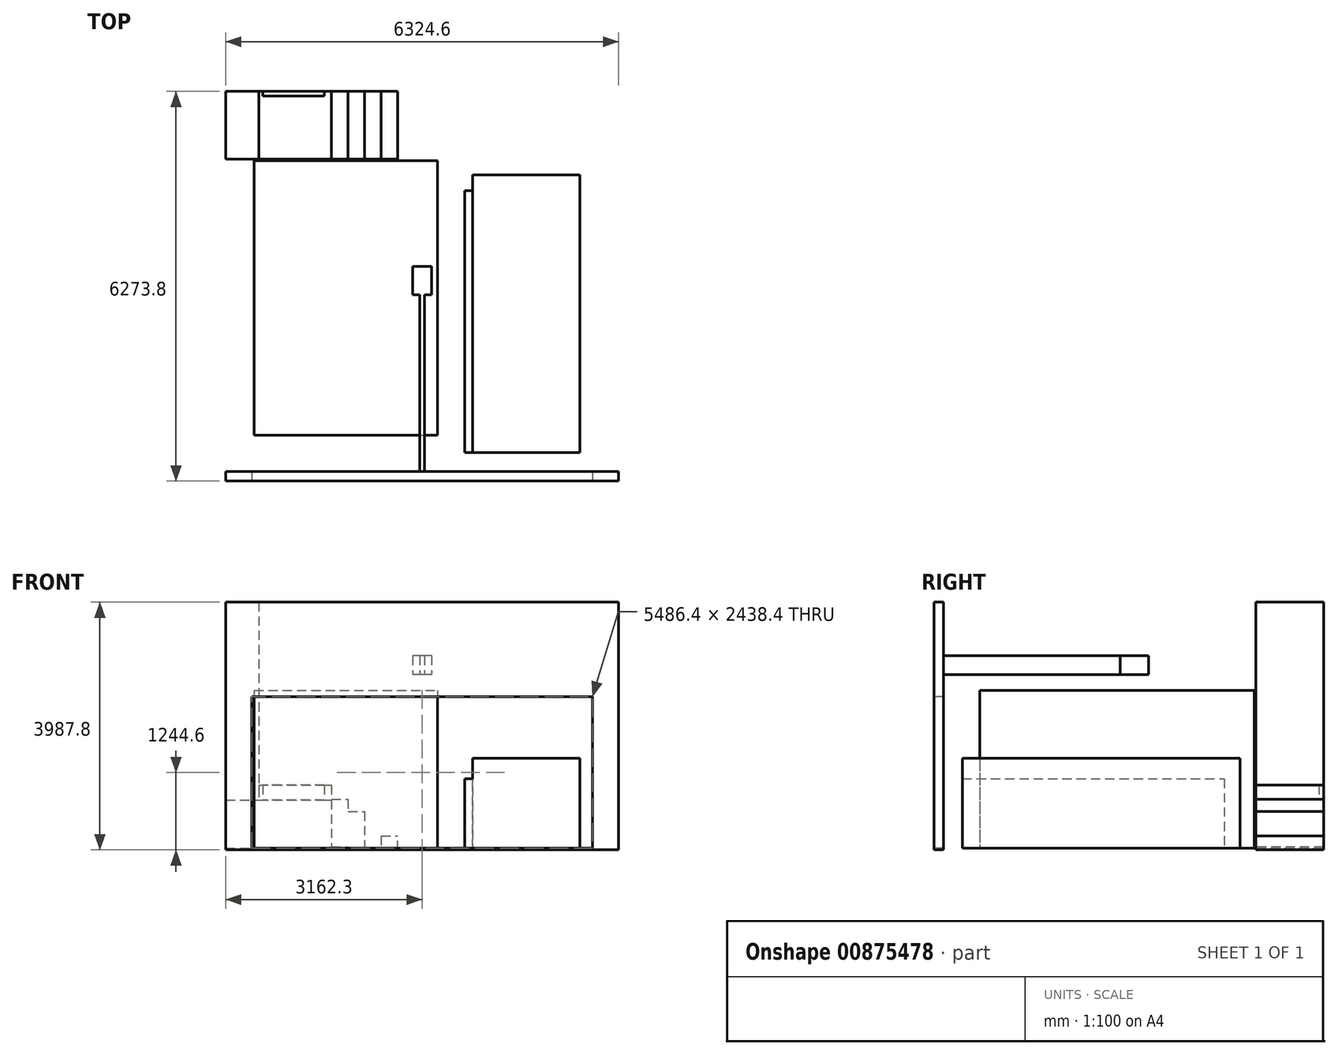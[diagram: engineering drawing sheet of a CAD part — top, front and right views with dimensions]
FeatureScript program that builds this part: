
annotation { "Feature Type Name" : "Feature", "Feature Type Description" : "" }
export const myFeature = defineFeature(function(context is Context, id is Id, definition is map)
    precondition{}
    {
        {
            var Q0;
            Q0=qCreatedBy(makeId("Top.planeOp"),FACE);
            var sketch = newSketch(context, id + "F0", { "sketchPlane" : qUnion([Q0])});
            skLineSegment(sketch, "E0.bottom", {"start": v(-3162.3, 3098.8) * mm, "end": v(3162.3, 3098.8) * mm});
            skLineSegment(sketch, "E0.top", {"start": v(-3162.3, -3098.8) * mm, "end": v(3162.3, -3098.8) * mm});
            skLineSegment(sketch, "E0.left", {"start": v(-3162.3, 3098.8) * mm, "end": v(-3162.3, -3098.8) * mm});
            skLineSegment(sketch, "E0.right", {"start": v(3162.3, 3098.8) * mm, "end": v(3162.3, -3098.8) * mm});
            skLineSegment(sketch, "E1.bottom", {"start": v(-3162.3, 3098.8) * mm, "end": v(-2628.9, 3098.8) * mm});
            skLineSegment(sketch, "E1.top", {"start": v(-3162.3, 2006.6) * mm, "end": v(-2628.9, 2006.6) * mm});
            skLineSegment(sketch, "E1.left", {"start": v(-3162.3, 3098.8) * mm, "end": v(-3162.3, 2006.6) * mm});
            skLineSegment(sketch, "E1.right", {"start": v(-2628.9, 3098.8) * mm, "end": v(-2628.9, 2006.6) * mm});
            skLineSegment(sketch, "E2.bottom", {"start": v(-2628.9, 2006.6) * mm, "end": v(-393.7, 2006.6) * mm});
            skLineSegment(sketch, "E2.top", {"start": v(-2628.9, 3098.8) * mm, "end": v(-393.7, 3098.8) * mm});
            skLineSegment(sketch, "E2.left", {"start": v(-2628.9, 2006.6) * mm, "end": v(-2628.9, 3098.8) * mm});
            skLineSegment(sketch, "E2.right", {"start": v(-393.7, 2006.6) * mm, "end": v(-393.7, 3098.8) * mm});
            skLineSegment(sketch, "E3.bottom", {"start": v(-1460.5, 3098.8) * mm, "end": v(-393.7, 3098.8) * mm});
            skLineSegment(sketch, "E3.top", {"start": v(-1460.5, 2006.6) * mm, "end": v(-393.7, 2006.6) * mm});
            skLineSegment(sketch, "E3.left", {"start": v(-1460.5, 3098.8) * mm, "end": v(-1460.5, 2006.6) * mm});
            skLineSegment(sketch, "E3.right", {"start": v(-393.7, 3098.8) * mm, "end": v(-393.7, 2006.6) * mm});
            skLineSegment(sketch, "E4.bottom", {"start": v(2743.2, -3022.6) * mm, "end": v(-2743.2, -3022.6) * mm});
            skLineSegment(sketch, "E4.top", {"start": v(2743.2, -3175) * mm, "end": v(-2743.2, -3175) * mm});
            skLineSegment(sketch, "E4.left", {"start": v(2743.2, -3022.6) * mm, "end": v(2743.2, -3175) * mm});
            skLineSegment(sketch, "E4.right", {"start": v(-2743.2, -3022.6) * mm, "end": v(-2743.2, -3175) * mm});
            skPoint(sketch, "E4.middle", {"position": v(0, -3098.8) * mm});
            skLineSegment(sketch, "E5.bottom", {"start": v(3238.5, -2006.6) * mm, "end": v(3086.1, -2006.6) * mm});
            skLineSegment(sketch, "E5.top", {"start": v(3238.5, -2921) * mm, "end": v(3086.1, -2921) * mm});
            skLineSegment(sketch, "E5.left", {"start": v(3238.5, -2006.6) * mm, "end": v(3238.5, -2921) * mm});
            skLineSegment(sketch, "E5.right", {"start": v(3086.1, -2006.6) * mm, "end": v(3086.1, -2921) * mm});
            skPoint(sketch, "E5.middle", {"position": v(3162.3, -2463.8) * mm});
            skLineSegment(sketch, "E6.bottom", {"start": v(-1576.66, 3175) * mm, "end": v(-2567.26, 3175) * mm});
            skLineSegment(sketch, "E6.top", {"start": v(-1576.66, 3022.6) * mm, "end": v(-2567.26, 3022.6) * mm});
            skLineSegment(sketch, "E6.left", {"start": v(-1576.66, 3175) * mm, "end": v(-1576.66, 3022.6) * mm});
            skLineSegment(sketch, "E6.right", {"start": v(-2567.26, 3175) * mm, "end": v(-2567.26, 3022.6) * mm});
            skPoint(sketch, "E6.middle", {"position": v(-2071.96, 3098.8) * mm});
            skLineSegment(sketch, "E7", {"start": v(-1193.8, 3098.8) * mm, "end": v(-1193.8, 2006.6) * mm});
            skLineSegment(sketch, "E8", {"start": v(-927.1, 3098.8) * mm, "end": v(-927.1, 2006.6) * mm});
            skLineSegment(sketch, "E9", {"start": v(-660.4, 2006.6) * mm, "end": v(-660.4, 3098.8) * mm});
            skSolve(sketch);
        }
        {
            var Q0;
            {var subQ3=sQuery(id+"F0.wireOp",EDGE,"E1.top");Q0=makeQuery(id+"F0.imprint","IMPRINT",FACE,{"disambiguationData":[TD([[makeQuery(id+"F0.imprint","IMPRINT",EDGE,{"derivedFrom":subQ3}),-1.0]])]});}
            var Q1;
            {var subQ4=sQuery(id+"F0.wireOp",EDGE,"E1.top");Q1=makeQuery(id+"F0.imprint","IMPRINT",FACE,{"disambiguationData":[TD([[makeQuery(id+"F0.imprint","IMPRINT",EDGE,{"derivedFrom":subQ4}),1.0]])]});}
            var Q2;
            {var subQ1=sQuery(id+"F0.wireOp",EDGE,"E1.right");Q2=makeQuery(id+"F0.imprint","IMPRINT",FACE,{"disambiguationData":[TD([[makeQuery(id+"F0.imprint","IMPRINT",EDGE,{"derivedFrom":subQ1}),1.0]])]});}
            var Q3;
            {var subQ0=sQuery(id+"F0.wireOp",EDGE,"E3.left");Q3=makeQuery(id+"F0.imprint","IMPRINT",FACE,{"disambiguationData":[TD([[makeQuery(id+"F0.imprint","IMPRINT",EDGE,{"derivedFrom":subQ0}),1.0]])]});}
            var Q4;
            {var subQ0=sQuery(id+"F0.wireOp",EDGE,"E7");Q4=makeQuery(id+"F0.imprint","IMPRINT",FACE,{"disambiguationData":[TD([[makeQuery(id+"F0.imprint","IMPRINT",EDGE,{"derivedFrom":subQ0}),1.0]])]});}
            var Q5;
            {var subQ0=sQuery(id+"F0.wireOp",EDGE,"E8");Q5=makeQuery(id+"F0.imprint","IMPRINT",FACE,{"disambiguationData":[TD([[makeQuery(id+"F0.imprint","IMPRINT",EDGE,{"derivedFrom":subQ0}),1.0]])]});}
            var Q6;
            {var subQ0=sQuery(id+"F0.wireOp",EDGE,"E2.right");Q6=makeQuery(id+"F0.imprint","IMPRINT",FACE,{"disambiguationData":[TD([[makeQuery(id+"F0.imprint","IMPRINT",EDGE,{"derivedFrom":subQ0}),1.0]])]});}
            var Q7;
            {var subQ5=sQuery(id+"F0.wireOp",EDGE,"E6.top");Q7=makeQuery(id+"F0.imprint","IMPRINT",FACE,{"disambiguationData":[TD([[makeQuery(id+"F0.imprint","IMPRINT",EDGE,{"derivedFrom":subQ5}),-1.0]])]});}
            extrude(context, id + "F1", {"entities" : qUnion([Q0, Q1, Q2, Q3, Q4, Q5, Q6, Q7]), "oppositeDirection" : true, "depth" : 25.4 * mm, "offsetDistance" : 25.4 * mm});
        }
        {
            var Q0;
            {var subQ4=sQuery(id+"F0.wireOp",EDGE,"E1.top");Q0=makeQuery(id+"F0.imprint","IMPRINT",FACE,{"disambiguationData":[TD([[makeQuery(id+"F0.imprint","IMPRINT",EDGE,{"derivedFrom":subQ4}),1.0]])]});}
            extrude(context, id + "F2", {"entities" : qUnion([Q0]), "depth" : 3962.4 * mm, "offsetDistance" : 25.4 * mm, "hasSecondDirection" : true, "secondDirectionOppositeDirection" : false, "secondDirectionDepth" : 774.7 * mm});
        }
        {
            var Q0;
            {var subQ1=sQuery(id+"F0.wireOp",EDGE,"E1.right");Q0=makeQuery(id+"F0.imprint","IMPRINT",FACE,{"disambiguationData":[TD([[makeQuery(id+"F0.imprint","IMPRINT",EDGE,{"derivedFrom":subQ1}),1.0]])]});}
            extrude(context, id + "F3", {"entities" : qUnion([Q0]), "depth" : 1016 * mm, "offsetDistance" : 25.4 * mm, "hasSecondDirection" : true, "secondDirectionOppositeDirection" : false, "secondDirectionDepth" : 774.7 * mm});
        }
        {
            var Q0;
            {var subQ0=sQuery(id+"F0.wireOp",EDGE,"E3.left");Q0=makeQuery(id+"F0.imprint","IMPRINT",FACE,{"disambiguationData":[TD([[makeQuery(id+"F0.imprint","IMPRINT",EDGE,{"derivedFrom":subQ0}),1.0]])]});}
            extrude(context, id + "F4", {"entities" : qUnion([Q0]), "operationType" : NewBodyOperationType.ADD, "depth" : 787.4 * mm, "offsetDistance" : 25.4 * mm, "hasSecondDirection" : true, "secondDirectionOppositeDirection" : false, "secondDirectionDepth" : ((31 - 7.75) - 1) * mm});
        }
        {
            var Q0;
            {var subQ0=sQuery(id+"F0.wireOp",EDGE,"E7");Q0=makeQuery(id+"F0.imprint","IMPRINT",FACE,{"disambiguationData":[TD([[makeQuery(id+"F0.imprint","IMPRINT",EDGE,{"derivedFrom":subQ0}),1.0]])]});}
            extrude(context, id + "F5", {"entities" : qUnion([Q0]), "operationType" : NewBodyOperationType.ADD, "depth" : 590.55 * mm, "offsetDistance" : 25.4 * mm, "hasSecondDirection" : true, "secondDirectionOppositeDirection" : false, "secondDirectionDepth" : (31 - (2 * 7.75) - 1) * mm});
        }
        {
            var Q0;
            {var subQ0=sQuery(id+"F0.wireOp",EDGE,"E8");Q0=makeQuery(id+"F0.imprint","IMPRINT",FACE,{"disambiguationData":[TD([[makeQuery(id+"F0.imprint","IMPRINT",EDGE,{"derivedFrom":subQ0}),1.0]])]});}
            extrude(context, id + "F6", {"entities" : qUnion([Q0]), "operationType" : NewBodyOperationType.ADD, "depth" : (31 - (7.75 * 2)) * mm, "offsetDistance" : 25.4 * mm, "hasSecondDirection" : true, "secondDirectionOppositeDirection" : false, "secondDirectionDepth" : (31 - (7.75 * 3) - 1) * mm});
        }
        {
            var Q0;
            {var subQ0=sQuery(id+"F0.wireOp",EDGE,"E2.right");Q0=makeQuery(id+"F0.imprint","IMPRINT",FACE,{"disambiguationData":[TD([[makeQuery(id+"F0.imprint","IMPRINT",EDGE,{"derivedFrom":subQ0}),1.0]])]});}
            extrude(context, id + "F7", {"entities" : qUnion([Q0]), "operationType" : NewBodyOperationType.ADD, "depth" : 196.85 * mm, "offsetDistance" : 25.4 * mm});
        }
        {
            var Q0;
            Q0=makeQuery(id+"F1.opExtrude","CAP_FACE",FACE,{"disambiguationData":[OSD([sQuery(id+"F0.wireOp",EDGE,"E0.bottom"),sQuery(id+"F0.wireOp",EDGE,"E0.top"),sQuery(id+"F0.wireOp",EDGE,"E0.left"),sQuery(id+"F0.wireOp",EDGE,"E0.right"),sQuery(id+"F0.wireOp",EDGE,"E4.bottom"),sQuery(id+"F0.wireOp",EDGE,"E4.left"),sQuery(id+"F0.wireOp",EDGE,"E4.right"),sQuery(id+"F0.wireOp",EDGE,"E5.bottom"),sQuery(id+"F0.wireOp",EDGE,"E5.top"),sQuery(id+"F0.wireOp",EDGE,"E5.right")])],"isStart":true});
            var sketch = newSketch(context, id + "F8", { "sketchPlane" : qUnion([Q0])});
            skLineSegment(sketch, "E10.bottom", {"start": v(-2705.1, 1981.2) * mm, "end": v(247.65, 1981.2) * mm});
            skLineSegment(sketch, "E10.top", {"start": v(-2705.1, -2438.4) * mm, "end": v(247.65, -2438.4) * mm});
            skLineSegment(sketch, "E10.left", {"start": v(-2705.1, 1981.2) * mm, "end": v(-2705.1, -2438.4) * mm});
            skLineSegment(sketch, "E10.right", {"start": v(247.65, 1981.2) * mm, "end": v(247.65, -2438.4) * mm});
            skLineSegment(sketch, "E11.bottom", {"start": v(-2274.82, -2438.4) * mm, "end": v(-1792.22, -2438.4) * mm});
            skLineSegment(sketch, "E11.top", {"start": v(-2274.82, -2819.4) * mm, "end": v(-1792.22, -2819.4) * mm});
            skLineSegment(sketch, "E11.left", {"start": v(-2274.82, -2438.4) * mm, "end": v(-2274.82, -2819.4) * mm});
            skLineSegment(sketch, "E11.right", {"start": v(-1792.22, -2438.4) * mm, "end": v(-1792.22, -2819.4) * mm});
            skLineSegment(sketch, "E12.bottom", {"start": v(-665.22, -2438.4) * mm, "end": v(-182.62, -2438.4) * mm});
            skLineSegment(sketch, "E12.top", {"start": v(-665.22, -2819.4) * mm, "end": v(-182.62, -2819.4) * mm});
            skLineSegment(sketch, "E12.left", {"start": v(-665.22, -2438.4) * mm, "end": v(-665.22, -2819.4) * mm});
            skLineSegment(sketch, "E12.right", {"start": v(-182.62, -2438.4) * mm, "end": v(-182.62, -2819.4) * mm});
            skPoint(sketch, "E13", {"position": v(-1228.72, -2438.4) * mm});
            skLineSegment(sketch, "E14.top", {"start": v(-2274.82, 1981.2) * mm, "end": v(-1792.22, 1981.2) * mm});
            skLineSegment(sketch, "E14.left", {"start": v(-2274.82, -2438.4) * mm, "end": v(-2274.82, 1981.2) * mm});
            skLineSegment(sketch, "E14.right", {"start": v(-1792.22, -2438.4) * mm, "end": v(-1792.22, 1981.2) * mm});
            skLineSegment(sketch, "E15.top", {"start": v(-665.22, 1981.2) * mm, "end": v(-182.62, 1981.2) * mm});
            skLineSegment(sketch, "E15.left", {"start": v(-665.22, -2438.4) * mm, "end": v(-665.22, 1981.2) * mm});
            skLineSegment(sketch, "E15.right", {"start": v(-182.62, -2438.4) * mm, "end": v(-182.62, 1981.2) * mm});
            skSolve(sketch);
        }
        {
            var Q0;
            Q0=makeQuery(id+"F8.imprint","IMPRINT",FACE,{"disambiguationData":[TD([[makeQuery(id+"F8.imprint","IMPRINT",EDGE,{"derivedFrom":sQuery(id+"F8.wireOp",EDGE,"E10.bottom")}),-1.0]])]});
            var Q1;
            Q1=makeQuery(id+"F8.imprint","IMPRINT",FACE,{"disambiguationData":[TD([[makeQuery(id+"F8.imprint","IMPRINT",EDGE,{"derivedFrom":sQuery(id+"F8.wireOp",EDGE,"E12.bottom")}),1.0]])]});
            var Q2;
            Q2=makeQuery(id+"F8.imprint","IMPRINT",FACE,{"disambiguationData":[TD([[makeQuery(id+"F8.imprint","IMPRINT",EDGE,{"derivedFrom":sQuery(id+"F8.wireOp",EDGE,"E11.bottom")}),1.0]])]});
            extrude(context, id + "F9", {"entities" : qUnion([Q0, Q1, Q2]), "depth" : 2540 * mm, "offsetDistance" : 25.4 * mm});
        }
        {
            var Q0;
            Q0=makeQuery(id+"F1.opExtrude","CAP_FACE",FACE,{"disambiguationData":[OSD([sQuery(id+"F0.wireOp",EDGE,"E0.bottom"),sQuery(id+"F0.wireOp",EDGE,"E0.top"),sQuery(id+"F0.wireOp",EDGE,"E0.left"),sQuery(id+"F0.wireOp",EDGE,"E0.right"),sQuery(id+"F0.wireOp",EDGE,"E4.bottom"),sQuery(id+"F0.wireOp",EDGE,"E4.left"),sQuery(id+"F0.wireOp",EDGE,"E4.right"),sQuery(id+"F0.wireOp",EDGE,"E5.bottom"),sQuery(id+"F0.wireOp",EDGE,"E5.top"),sQuery(id+"F0.wireOp",EDGE,"E5.right")])],"isStart":true});
            var sketch = newSketch(context, id + "F10", { "sketchPlane" : qUnion([Q0])});
            skLineSegment(sketch, "E16.bottom", {"start": v(683.26, -2717.8) * mm, "end": v(2540, -2717.8) * mm});
            skLineSegment(sketch, "E16.top", {"start": v(683.26, 1498.6) * mm, "end": v(2540, 1498.6) * mm});
            skLineSegment(sketch, "E16.left", {"start": v(683.26, -2717.8) * mm, "end": v(683.26, 1498.6) * mm});
            skLineSegment(sketch, "E16.right", {"start": v(2540, -2717.8) * mm, "end": v(2540, 1498.6) * mm});
            skSolve(sketch);
        }
        {
            var Q0;
            {var subQ0=sQuery(id+"F10.wireOp",EDGE,"E16.bottom");Q0=makeQuery(id+"F10.imprint","IMPRINT",FACE,{"disambiguationData":[TD([[makeQuery(id+"F10.imprint","IMPRINT",EDGE,{"derivedFrom":subQ0}),1.0]])]});}
            var Q1;
            {var subQ0=sQuery(id+"F10.wireOp",EDGE,"E16.top");Q1=makeQuery(id+"F10.imprint","IMPRINT",FACE,{"disambiguationData":[TD([[makeQuery(id+"F10.imprint","IMPRINT",EDGE,{"derivedFrom":subQ0}),-1.0]])]});}
            extrude(context, id + "F11", {"entities" : qUnion([Q0, Q1]), "depth" : 1117.6 * mm, "offsetDistance" : 25.4 * mm});
        }
        {
            var Q0;
            Q0=makeQuery(id+"F1.opExtrude","CAP_FACE",FACE,{"disambiguationData":[OSD([sQuery(id+"F0.wireOp",EDGE,"E0.bottom"),sQuery(id+"F0.wireOp",EDGE,"E0.top"),sQuery(id+"F0.wireOp",EDGE,"E0.left"),sQuery(id+"F0.wireOp",EDGE,"E0.right"),sQuery(id+"F0.wireOp",EDGE,"E4.bottom"),sQuery(id+"F0.wireOp",EDGE,"E4.left"),sQuery(id+"F0.wireOp",EDGE,"E4.right"),sQuery(id+"F0.wireOp",EDGE,"E5.bottom"),sQuery(id+"F0.wireOp",EDGE,"E5.top"),sQuery(id+"F0.wireOp",EDGE,"E5.right")])],"isStart":true});
            var sketch = newSketch(context, id + "F12", { "sketchPlane" : qUnion([Q0])});
            skLineSegment(sketch, "E17.bottom", {"start": v(812.8, -2717.8) * mm, "end": v(2540, -2717.8) * mm});
            skLineSegment(sketch, "E17.top", {"start": v(812.8, 1752.6) * mm, "end": v(2540, 1752.6) * mm});
            skLineSegment(sketch, "E17.left", {"start": v(812.8, -2717.8) * mm, "end": v(812.8, 1752.6) * mm});
            skLineSegment(sketch, "E17.right", {"start": v(2540, -2717.8) * mm, "end": v(2540, 1752.6) * mm});
            skSolve(sketch);
        }
        {
            var Q0;
            Q0=makeQuery(id+"F12.imprint","IMPRINT",FACE,{"disambiguationData":[TD([[makeQuery(id+"F12.imprint","IMPRINT",EDGE,{"derivedFrom":sQuery(id+"F12.wireOp",EDGE,"E17.bottom")}),1.0]])]});
            extrude(context, id + "F13", {"entities" : qUnion([Q0]), "operationType" : NewBodyOperationType.ADD, "depth" : 1447.8 * mm, "offsetDistance" : 25.4 * mm});
        }
        {
            var Q0;
            Q0=makeQuery(id+"F1.opExtrude","CAP_FACE",FACE,{"disambiguationData":[OSD([sQuery(id+"F0.wireOp",EDGE,"E0.bottom"),sQuery(id+"F0.wireOp",EDGE,"E0.top"),sQuery(id+"F0.wireOp",EDGE,"E0.left"),sQuery(id+"F0.wireOp",EDGE,"E0.right"),sQuery(id+"F0.wireOp",EDGE,"E4.bottom"),sQuery(id+"F0.wireOp",EDGE,"E4.left"),sQuery(id+"F0.wireOp",EDGE,"E4.right"),sQuery(id+"F0.wireOp",EDGE,"E5.bottom"),sQuery(id+"F0.wireOp",EDGE,"E5.top"),sQuery(id+"F0.wireOp",EDGE,"E5.right")])],"isStart":true});
            var sketch = newSketch(context, id + "F14", { "sketchPlane" : qUnion([Q0])});
            skLineSegment(sketch, "E18.bottom", {"start": v(38.1, -177.8) * mm, "end": v(-38.1, -177.8) * mm});
            skLineSegment(sketch, "E18.top", {"start": v(38.1, -3022.6) * mm, "end": v(-38.1, -3022.6) * mm});
            skLineSegment(sketch, "E18.left", {"start": v(38.1, -177.8) * mm, "end": v(38.1, -3022.6) * mm});
            skLineSegment(sketch, "E18.right", {"start": v(-38.1, -177.8) * mm, "end": v(-38.1, -3022.6) * mm});
            skPoint(sketch, "E18.middle", {"position": v(0, -1600.2) * mm});
            skPoint(sketch, "E18.middle.positionSnap0", {"position": v(0, -3022.6) * mm});
            skPoint(sketch, "E18.centerSnap0", {"position": v(0, -3022.6) * mm});
            skLineSegment(sketch, "E19.bottom", {"start": v(152.4, -177.8) * mm, "end": v(-152.4, -177.8) * mm});
            skLineSegment(sketch, "E19.top", {"start": v(152.4, 279.4) * mm, "end": v(-152.4, 279.4) * mm});
            skLineSegment(sketch, "E19.left", {"start": v(152.4, -177.8) * mm, "end": v(152.4, 279.4) * mm});
            skLineSegment(sketch, "E19.right", {"start": v(-152.4, -177.8) * mm, "end": v(-152.4, 279.4) * mm});
            skPoint(sketch, "E19.middle", {"position": v(0, 50.8) * mm});
            skPoint(sketch, "E19.middle.positionSnap0", {"position": v(0, -177.8) * mm});
            skPoint(sketch, "E19.cornerSnap0", {"position": v(0, -177.8) * mm});
            skPoint(sketch, "E19.centerSnap0", {"position": v(0, -177.8) * mm});
            skSolve(sketch);
        }
        {
            var Q0;
            Q0 = qSketchRegion(id + "F14", true);
            extrude(context, id + "F15", {"entities" : qUnion([Q0]), "depth" : 3098.8 * mm, "offsetDistance" : 25.4 * mm, "hasSecondDirection" : true, "secondDirectionOppositeDirection" : false, "secondDirectionDepth" : 2794 * mm});
        }
        {
            var Q0;
            Q0=makeQuery(id+"F1.opExtrude","CAP_FACE",FACE,{"disambiguationData":[OSD([sQuery(id+"F0.wireOp",EDGE,"E0.bottom"),sQuery(id+"F0.wireOp",EDGE,"E0.top"),sQuery(id+"F0.wireOp",EDGE,"E0.left"),sQuery(id+"F0.wireOp",EDGE,"E0.right"),sQuery(id+"F0.wireOp",EDGE,"E4.bottom"),sQuery(id+"F0.wireOp",EDGE,"E4.left"),sQuery(id+"F0.wireOp",EDGE,"E4.right"),sQuery(id+"F0.wireOp",EDGE,"E5.bottom"),sQuery(id+"F0.wireOp",EDGE,"E5.top"),sQuery(id+"F0.wireOp",EDGE,"E5.right")])],"isStart":true});
            var sketch = newSketch(context, id + "F16", { "sketchPlane" : qUnion([Q0])});
            skLineSegment(sketch, "E20.bottom", {"start": v(-2743.2, -3022.6) * mm, "end": v(-3162.3, -3022.6) * mm});
            skLineSegment(sketch, "E20.top", {"start": v(-2743.2, -3175) * mm, "end": v(-3162.3, -3175) * mm});
            skLineSegment(sketch, "E20.left", {"start": v(-2743.2, -3022.6) * mm, "end": v(-2743.2, -3175) * mm});
            skLineSegment(sketch, "E20.right", {"start": v(-3162.3, -3022.6) * mm, "end": v(-3162.3, -3175) * mm});
            skPoint(sketch, "E20.middle", {"position": v(-2952.75, -3098.8) * mm});
            skLineSegment(sketch, "E21.bottom", {"start": v(2743.2, -3022.6) * mm, "end": v(3162.3, -3022.6) * mm});
            skLineSegment(sketch, "E21.top", {"start": v(2743.2, -3175) * mm, "end": v(3162.3, -3175) * mm});
            skLineSegment(sketch, "E21.left", {"start": v(2743.2, -3022.6) * mm, "end": v(2743.2, -3175) * mm});
            skLineSegment(sketch, "E21.right", {"start": v(3162.3, -3022.6) * mm, "end": v(3162.3, -3175) * mm});
            skPoint(sketch, "E21.middle", {"position": v(2952.75, -3098.8) * mm});
            skLineSegment(sketch, "E22.bottom", {"start": v(2743.2, -3022.6) * mm, "end": v(-2743.2, -3022.6) * mm});
            skLineSegment(sketch, "E22.top", {"start": v(2743.2, -3175) * mm, "end": v(-2743.2, -3175) * mm});
            skSolve(sketch);
        }
        {
            var Q0;
            {var subQ0=sQuery(id+"F16.wireOp",EDGE,"E20.top");Q0=makeQuery(id+"F16.imprint","IMPRINT",FACE,{"disambiguationData":[TD([[makeQuery(id+"F16.imprint","IMPRINT",EDGE,{"derivedFrom":subQ0}),-1.0]])]});}
            var Q1;
            {var subQ0=sQuery(id+"F16.wireOp",EDGE,"E20.bottom");Q1=makeQuery(id+"F16.imprint","IMPRINT",FACE,{"disambiguationData":[TD([[makeQuery(id+"F16.imprint","IMPRINT",EDGE,{"derivedFrom":subQ0}),1.0]])]});}
            var Q2;
            {var subQ0=sQuery(id+"F16.wireOp",EDGE,"E21.top");Q2=makeQuery(id+"F16.imprint","IMPRINT",FACE,{"disambiguationData":[TD([[makeQuery(id+"F16.imprint","IMPRINT",EDGE,{"derivedFrom":subQ0}),1.0]])]});}
            var Q3;
            {var subQ0=sQuery(id+"F16.wireOp",EDGE,"E21.bottom");Q3=makeQuery(id+"F16.imprint","IMPRINT",FACE,{"disambiguationData":[TD([[makeQuery(id+"F16.imprint","IMPRINT",EDGE,{"derivedFrom":subQ0}),-1.0]])]});}
            var Q4;
            {var subQ1=sQuery(id+"F16.wireOp",EDGE,"E22.bottom");Q4=makeQuery(id+"F16.imprint","IMPRINT",FACE,{"disambiguationData":[TD([[makeQuery(id+"F16.imprint","IMPRINT",EDGE,{"derivedFrom":subQ1}),1.0]])]});}
            extrude(context, id + "F17", {"entities" : qUnion([Q0, Q1, Q2, Q3, Q4]), "depth" : 3962.4 * mm, "offsetDistance" : 25.4 * mm, "hasSecondDirection" : true, "secondDirectionOppositeDirection" : true, "secondDirectionDepth" : 25.4 * mm});
        }
        {
            var Q0;
            {var subQ1=sQuery(id+"F16.wireOp",EDGE,"E22.bottom");Q0=makeQuery(id+"F16.imprint","IMPRINT",FACE,{"disambiguationData":[TD([[makeQuery(id+"F16.imprint","IMPRINT",EDGE,{"derivedFrom":subQ1}),1.0]])]});}
            extrude(context, id + "F18", {"entities" : qUnion([Q0]), "operationType" : NewBodyOperationType.REMOVE, "depth" : 2438.4 * mm, "offsetDistance" : 25.4 * mm});
        }
    });
